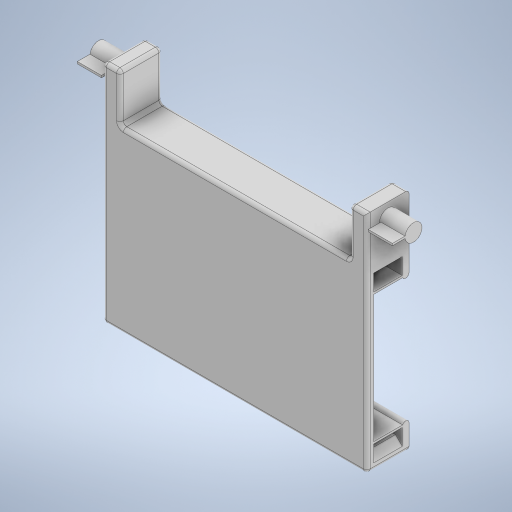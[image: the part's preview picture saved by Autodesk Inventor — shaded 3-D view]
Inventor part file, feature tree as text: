
AUTODESK INVENTOR PART (.ipt)
format: ipt  version: 2024 (Build 280153000, 153)  size: 410,112 bytes
history: native  units: mm
features: extrude x8, sketch x8, fillet x6, mirror x4, chamfer x1
ambient origin geometry x8: Origin, YZ Plane, XZ Plane, XY Plane, X Axis, Y Axis, Z Axis, Center Point
bodies: Volumenkörper1 (feature_tree)
feature tree (27):
  extrude  "Extrusion1"  Depth=5.2mm TaperAngle=0.0deg
  extrude  "Extrusion2"  Depth=36.7mm
  extrude  "Extrusion3"  Depth=1.0mm
  extrude  "Extrusion7"  Depth=2.0mm
  mirror  "Spiegeln2"
  extrude  "Extrusion8"  Depth=2.0mm
  extrude  "Extrusion9"  Depth=1.5mm
  mirror  "Spiegeln3"
  extrude  "Extrusion10"  Depth=0.3mm
  mirror  "Spiegeln4"
  extrude  "Extrusion11"  Depth=0.25mm TaperAngle=0.0deg
  mirror  "Spiegeln5"
  fillet  "Rundung1"  Radius=2.0mm
  fillet  "Rundung2"  Radius=2.5mm
  fillet  "Rundung3"  Radius=3.75mm
  fillet  "Rundung4"  Radius=0.3mm
  chamfer  "Fasen1"  Distance=0.4mm
  fillet  "Rundung5"  Radius=10.0mm
  fillet  "Rundung6"  Radius=0.3mm
  sketch  "Skizze1"  dims[d2=1.0mm d3=0.0mm d6=5.2mm d7=0.0mm]
  sketch  "Skizze2"  dims[d11=1.0mm d12=0.0mm d24=36.7mm]
  sketch  "Skizze3"  dims[d25=22.1mm d26=1.0mm]
  sketch  "Skizze7"  dims[d27=0.0mm d30=2.0mm]
  sketch  "Skizze8"  dims[d31=2.0mm d35=2.0mm]
  sketch  "Skizze9"  dims[d36=2.0mm d38=1.5mm]
  sketch  "Skizze11"  dims[d39=2.5mm d40=0.3mm d41=-8.726646mm]
  sketch  "Skizze12"  dims[d42=2.5mm d43=7.0mm d44=0.0mm d45=2.0mm d46=2.5mm d47=3.75mm d48=0.0mm d50=0.3mm d51=0.4mm d52=10.0mm d53=0.0mm d54=0.3mm d55=0.15mm d56=0.15mm d57=0.2mm d58=0.0mm d59=0.0mm d60=0.5mm d61=0.5mm d62=0.5mm d63=0.5mm d64=1.0mm d65=2.0mm d66=45.0deg d67=0.5mm d68=0.25mm d69=0.0mm d70=0.0mm d71=0.0mm]
